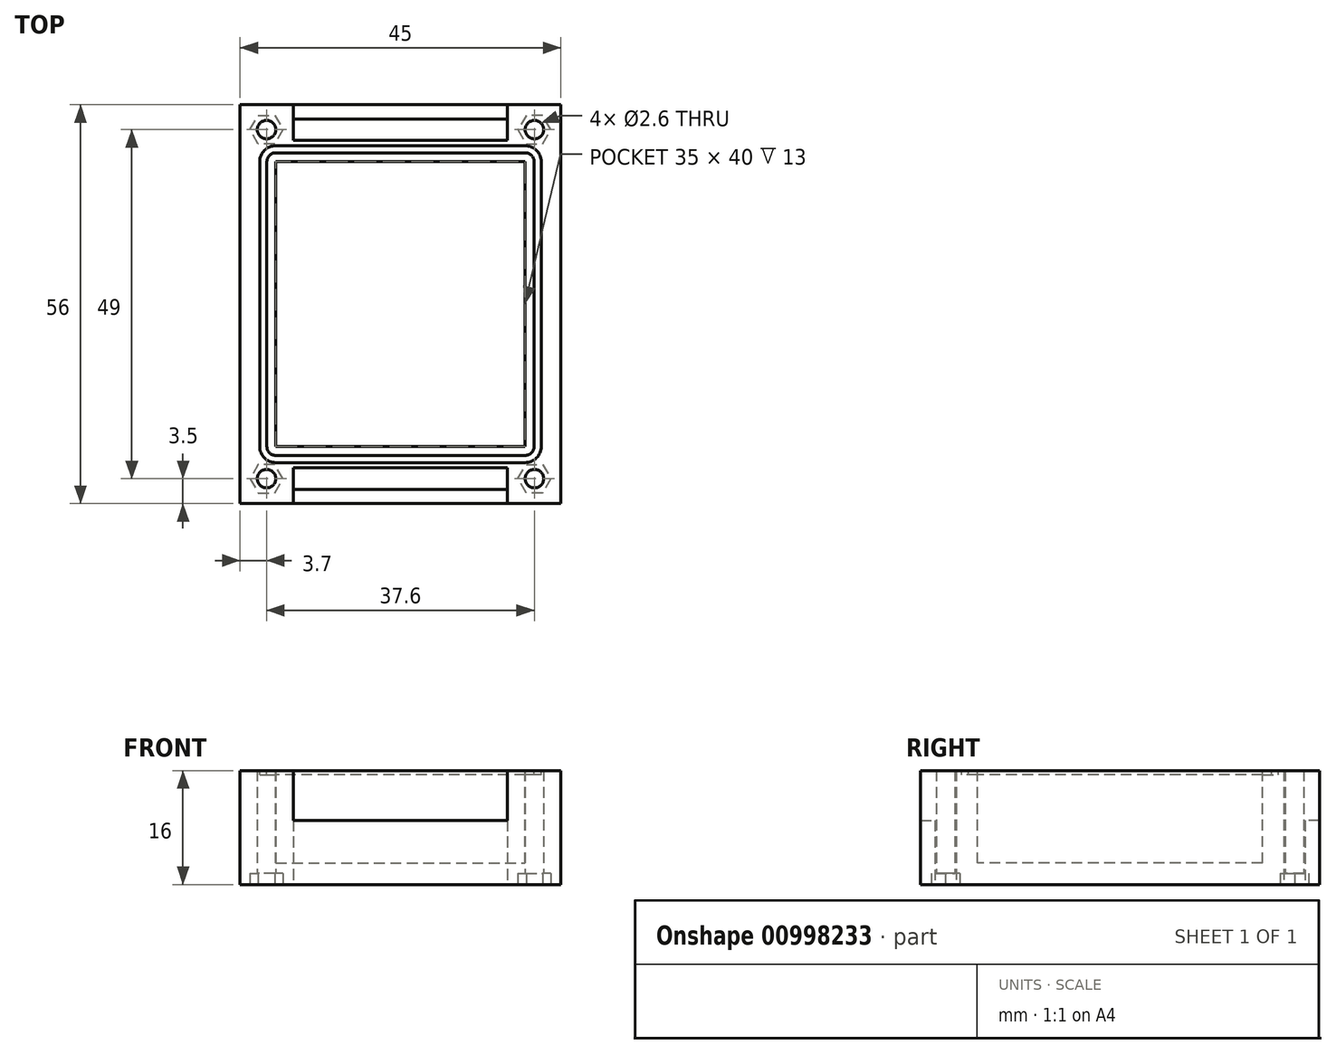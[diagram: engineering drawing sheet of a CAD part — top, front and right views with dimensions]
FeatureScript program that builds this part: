
annotation { "Feature Type Name" : "Feature", "Feature Type Description" : "" }
export const myFeature = defineFeature(function(context is Context, id is Id, definition is map)
    precondition{}
    {
        {
            var Q0;
            Q0=qCreatedBy(makeId("Top.planeOp"),FACE);
            var Q1;
            Q1=qCreatedBy(makeId("Top.planeOp"),FACE);
            var sketch = newSketch(context, id + "F0", { "sketchPlane" : qUnion([Q0, Q1])});
            skLineSegment(sketch, "E0", {"start": v(0, 23) * mm, "end": v(15, 23) * mm});
            skLineSegment(sketch, "E1", {"start": v(22.5, 28) * mm, "end": v(22.5, 0) * mm});
            skLineSegment(sketch, "E2", {"start": v(0, 23) * mm, "end": v(0, 0) * mm});
            skLineSegment(sketch, "E3", {"start": v(0, 28) * mm, "end": v(0, 26) * mm});
            skLineSegment(sketch, "E4", {"start": v(0, 26) * mm, "end": v(15, 26) * mm});
            skLineSegment(sketch, "E5", {"start": v(15, 23) * mm, "end": v(15, 26) * mm});
            skLineSegment(sketch, "E6", {"start": v(0, 28) * mm, "end": v(22.5, 28) * mm});
            skLineSegment(sketch, "E7", {"start": v(22.5, 0) * mm, "end": v(0, 0) * mm});
            skPoint(sketch, "E8.orphan", {"position": v(0, 0) * mm});
            skSolve(sketch);
        }
        {
            var Q0;
            Q0 = qSketchRegion(id + "F0", true);
            extrude(context, id + "F1", {"entities" : qUnion([Q0]), "depth" : 16 * mm, "offsetDistance" : 25 * mm});
        }
        {
            var Q0;
            Q0=makeQuery(id+"F1.opExtrude","CAP_FACE",FACE,{"disambiguationData":[OSD([sQuery(id+"F0.wireOp",EDGE,"E0"),sQuery(id+"F0.wireOp",EDGE,"zLziVwUA-pqAk-qgk8-8UCK-iLvItPBVNLMh"),sQuery(id+"F0.wireOp",EDGE,"wFU1Dp7x-DsTY-6w94-6RtG-82Ve4ZeFUhQ2"),sQuery(id+"F0.wireOp",EDGE,"E1"),sQuery(id+"F0.wireOp",EDGE,"1tPFTLfK-o8Uq-jivp-b70F-p9IYyag1Aok2"),sQuery(id+"F0.wireOp",EDGE,"YqrB6EEW-OV6K-1aBH-CTyA-Jv0BLjLknPQv"),sQuery(id+"F0.wireOp",EDGE,"oTJ8Ghu3-OfHO-qnZb-d6aa-sj9z2I1jH8fg"),sQuery(id+"F0.wireOp",EDGE,"E2")])],"isStart":false});
            var sketch = newSketch(context, id + "F2", { "sketchPlane" : qUnion([Q0])});
            skLineSegment(sketch, "E9.bottom", {"start": v(0, 20) * mm, "end": v(17.5, 20) * mm});
            skLineSegment(sketch, "E9.top", {"start": v(0, 0) * mm, "end": v(17.5, 0) * mm});
            skLineSegment(sketch, "E9.left", {"start": v(0, 20) * mm, "end": v(0, 0) * mm});
            skLineSegment(sketch, "E9.right", {"start": v(17.5, 20) * mm, "end": v(17.5, 0) * mm});
            skSolve(sketch);
        }
        {
            var Q0;
            Q0 = qSketchRegion(id + "F2", true);
            extrude(context, id + "F3", {"entities" : qUnion([Q0]), "operationType" : NewBodyOperationType.REMOVE, "oppositeDirection" : true, "depth" : 13 * mm, "offsetDistance" : 25 * mm});
        }
        {
            var Q0;
            {var subQ0=makeQuery(id+"F1.opExtrude","CAP_FACE",FACE,{"disambiguationData":[OSD([sQuery(id+"F0.wireOp",EDGE,"E0"),sQuery(id+"F0.wireOp",EDGE,"zLziVwUA-pqAk-qgk8-8UCK-iLvItPBVNLMh"),sQuery(id+"F0.wireOp",EDGE,"wFU1Dp7x-DsTY-6w94-6RtG-82Ve4ZeFUhQ2"),sQuery(id+"F0.wireOp",EDGE,"E1"),sQuery(id+"F0.wireOp",EDGE,"1tPFTLfK-o8Uq-jivp-b70F-p9IYyag1Aok2"),sQuery(id+"F0.wireOp",EDGE,"YqrB6EEW-OV6K-1aBH-CTyA-Jv0BLjLknPQv"),sQuery(id+"F0.wireOp",EDGE,"oTJ8Ghu3-OfHO-qnZb-d6aa-sj9z2I1jH8fg"),sQuery(id+"F0.wireOp",EDGE,"E2")])],"isStart":false});Q0=makeQuery(id+"F12.boolean.opBoolean","MERGE",FACE,{"derivedFrom":[subQ0,makeQuery(id+"F12.opPattern","COPY",FACE,{"derivedFrom":subQ0,"instanceName":"1"})]});}
            var sketch = newSketch(context, id + "F4", { "sketchPlane" : qUnion([Q0])});
            skLineSegment(sketch, "E10.bottom", {"start": v(0, 22.25) * mm, "end": v(17.5, 22.25) * mm});
            skArc(sketch, "E11", {"start": v(18.75, 20) * mm, "mid": v(18.38, 20.88) * mm, "end": v(17.5, 21.25) * mm});
            skArc(sketch, "E12", {"start": v(19.75, 20) * mm, "mid": v(19.1, 21.6) * mm, "end": v(17.5, 22.25) * mm});
            skLineSegment(sketch, "E13", {"start": v(17.5, 21.25) * mm, "end": v(0, 21.25) * mm});
            skLineSegment(sketch, "E14", {"start": v(18.75, 20) * mm, "end": v(18.75, 0) * mm});
            skLineSegment(sketch, "E15", {"start": v(19.75, 20) * mm, "end": v(19.75, 0) * mm});
            skLineSegment(sketch, "E16", {"start": v(0, 22.25) * mm, "end": v(0, 21.25) * mm});
            skLineSegment(sketch, "E17", {"start": v(19.75, 0) * mm, "end": v(18.75, 0) * mm});
            skSolve(sketch);
        }
        {
            var Q0;
            Q0 = qSketchRegion(id + "F4", true);
            extrude(context, id + "F5", {"entities" : qUnion([Q0]), "operationType" : NewBodyOperationType.REMOVE, "oppositeDirection" : true, "depth" : .6 * mm, "offsetDistance" : 25 * mm});
        }
        {
            var Q0;
            {var subQ0=makeQuery(id+"F1.opExtrude","CAP_FACE",FACE,{"disambiguationData":[OSD([sQuery(id+"F0.wireOp",EDGE,"E0"),sQuery(id+"F0.wireOp",EDGE,"E1"),sQuery(id+"F0.wireOp",EDGE,"oTJ8Ghu3-OfHO-qnZb-d6aa-sj9z2I1jH8fg"),sQuery(id+"F0.wireOp",EDGE,"E2"),sQuery(id+"F0.wireOp",EDGE,"E3"),sQuery(id+"F0.wireOp",EDGE,"E4"),sQuery(id+"F0.wireOp",EDGE,"E5"),sQuery(id+"F0.wireOp",EDGE,"Zl3f4Z5Q-yM6C-ffHE-Njlt-vzNsvvNb8iaK"),sQuery(id+"F0.wireOp",EDGE,"fbViNYte-NkZI-zoeq-aq0m-hkNtb6oqrqdO"),sQuery(id+"F0.wireOp",EDGE,"qfmNc8zk-el2u-9pkF-pBeT-ObQ48wad9USP"),sQuery(id+"F0.wireOp",EDGE,"E6"),sQuery(id+"F0.wireOp",EDGE,"2uNglbtt-g0ze-XEj7-sdbv-NYKCwFkJiIXs")])],"isStart":true});Q0=makeQuery(id+"F12.boolean.opBoolean","MERGE",FACE,{"derivedFrom":[subQ0,makeQuery(id+"F12.opPattern","COPY",FACE,{"derivedFrom":subQ0,"instanceName":"1"})]});}
            var sketch = newSketch(context, id + "F6", { "sketchPlane" : qUnion([Q0])});
            skCircle(sketch, "E18", {"center": v(18.8, -24.5) * mm, "radius": 2.3 * mm, "construction": true});
            skLineSegment(sketch, "E19.0", {"start": v(21.1, -24.5) * mm, "end": v(19.95, -26.5) * mm});
            skLineSegment(sketch, "E19.1", {"start": v(19.95, -26.5) * mm, "end": v(17.65, -26.5) * mm});
            skLineSegment(sketch, "E19.2", {"start": v(17.65, -26.5) * mm, "end": v(16.5, -24.5) * mm});
            skLineSegment(sketch, "E19.3", {"start": v(16.5, -24.5) * mm, "end": v(17.65, -22.5) * mm});
            skLineSegment(sketch, "E19.4", {"start": v(17.65, -22.5) * mm, "end": v(19.95, -22.5) * mm});
            skLineSegment(sketch, "E19.5", {"start": v(19.95, -22.5) * mm, "end": v(21.1, -24.5) * mm});
            skPoint(sketch, "E20", {"position": v(15, -24.5) * mm});
            skSolve(sketch);
        }
        {
            var Q0;
            Q0 = qSketchRegion(id + "F6", true);
            extrude(context, id + "F7", {"entities" : qUnion([Q0]), "operationType" : NewBodyOperationType.REMOVE, "oppositeDirection" : true, "depth" : 1.6 * mm, "offsetDistance" : 25 * mm});
        }
        {
            var Q0;
            {var subQ0=makeQuery(id+"F1.opExtrude","CAP_FACE",FACE,{"disambiguationData":[OSD([sQuery(id+"F0.wireOp",EDGE,"E0"),sQuery(id+"F0.wireOp",EDGE,"E1"),sQuery(id+"F0.wireOp",EDGE,"E2"),sQuery(id+"F0.wireOp",EDGE,"E3"),sQuery(id+"F0.wireOp",EDGE,"E4"),sQuery(id+"F0.wireOp",EDGE,"E5"),sQuery(id+"F0.wireOp",EDGE,"E6"),sQuery(id+"F0.wireOp",EDGE,"E7")])],"isStart":true});var subQ1=makeQuery(id+"F12.boolean.opBoolean","MERGE",FACE,{"derivedFrom":[subQ0,makeQuery(id+"F12.opPattern","COPY",FACE,{"derivedFrom":subQ0,"instanceName":"1"})]});Q0=makeQuery(id+"F13.boolean.opBoolean","MERGE",FACE,{"derivedFrom":[subQ1,makeQuery(id+"F13.opPattern","COPY",FACE,{"derivedFrom":subQ1,"instanceName":"1"})]});}
            var sketch = newSketch(context, id + "F8", { "sketchPlane" : qUnion([Q0])});
            skPoint(sketch, "E21", {"position": v(18.8, -24.5) * mm});
            skSolve(sketch);
        }
        {
            var Q0;
            Q0=sQuery(id+"F8.wireOp",VERTEX,"E21");
            var Q1;
            Q1=makeQuery(id+"F1.opExtrude","SWEPT_BODY",BODY,{"disambiguationData":[OSD([sQuery(id+"F0.wireOp",EDGE,"E0"),sQuery(id+"F0.wireOp",EDGE,"E1"),sQuery(id+"F0.wireOp",EDGE,"oTJ8Ghu3-OfHO-qnZb-d6aa-sj9z2I1jH8fg"),sQuery(id+"F0.wireOp",EDGE,"E2"),sQuery(id+"F0.wireOp",EDGE,"E3"),sQuery(id+"F0.wireOp",EDGE,"E4"),sQuery(id+"F0.wireOp",EDGE,"E5"),sQuery(id+"F0.wireOp",EDGE,"Zl3f4Z5Q-yM6C-ffHE-Njlt-vzNsvvNb8iaK"),sQuery(id+"F0.wireOp",EDGE,"fbViNYte-NkZI-zoeq-aq0m-hkNtb6oqrqdO"),sQuery(id+"F0.wireOp",EDGE,"qfmNc8zk-el2u-9pkF-pBeT-ObQ48wad9USP"),sQuery(id+"F0.wireOp",EDGE,"E6"),sQuery(id+"F0.wireOp",EDGE,"2uNglbtt-g0ze-XEj7-sdbv-NYKCwFkJiIXs")])]});
            hole(context, id + "F9", {"style" : HoleStyle.SIMPLE, "endStyle" : HoleEndStyle.THROUGH, "standardTappedOrClearance" : lookupTablePath({ "fit" : "Loose", "standard" : "ISO", "size" : "M2", "type" : "Clearance" }), "standardBlindInLast" : lookupTablePath({ "fit" : "Loose", "standard" : "ISO", "engagement" : "75%", "pitch" : "0.25 mm", "size" : "M2", "type" : "Clearance & tapped" }), "holeDiameter" : 2.6 * mm, "majorDiameter" : 5 * mm, "isTappedThrough" : true, "tappedDepth" : 12 * mm, "tapClearance" : 3, "locations" : qUnion([Q0]), "scope" : qUnion([Q1])});
        }
        {
            var Q0;
            {var subQ0=sQuery(id+"F0.wireOp",EDGE,"E7");var subQ1=sQuery(id+"F0.wireOp",EDGE,"E6");var subQ2=sQuery(id+"F0.wireOp",EDGE,"E5");var subQ3=sQuery(id+"F0.wireOp",EDGE,"E4");var subQ4=sQuery(id+"F0.wireOp",EDGE,"E0");var subQ5=sQuery(id+"F0.wireOp",EDGE,"E3");var subQ6=sQuery(id+"F0.wireOp",EDGE,"E1");var subQ7=sQuery(id+"F0.wireOp",EDGE,"E2");var subQ8=makeQuery(id+"F5.boolean.opBoolean","SPLIT",FACE,{"disambiguationData":[TD([makeQuery(id+"F1.opExtrude","SWEPT_FACE",FACE,{"disambiguationData":[OSD([subQ4])]})])],"derivedFrom":makeQuery(id+"F1.opExtrude","CAP_FACE",FACE,{"disambiguationData":[OSD([subQ4,subQ6,subQ7,subQ5,subQ3,subQ2,subQ1,subQ0])],"isStart":false})});var subQ9=makeQuery(id+"F12.boolean.opBoolean","MERGE",FACE,{"derivedFrom":[subQ8,makeQuery(id+"F12.opPattern","COPY",FACE,{"derivedFrom":subQ8,"instanceName":"1"})]});Q0=makeQuery(id+"F13.boolean.opBoolean","MERGE",FACE,{"derivedFrom":[subQ9,makeQuery(id+"F13.opPattern","COPY",FACE,{"derivedFrom":subQ9,"instanceName":"1"})]});}
            var sketch = newSketch(context, id + "F10", { "sketchPlane" : qUnion([Q0])});
            skLineSegment(sketch, "E22.bottom", {"start": v(0, 30.37) * mm, "end": v(15, 30.37) * mm});
            skLineSegment(sketch, "E22.top", {"start": v(0, 26) * mm, "end": v(15, 26) * mm});
            skLineSegment(sketch, "E22.left", {"start": v(0, 30.37) * mm, "end": v(0, 26) * mm});
            skLineSegment(sketch, "E22.right", {"start": v(15, 30.37) * mm, "end": v(15, 26) * mm});
            skSolve(sketch);
        }
        {
            var Q0;
            Q0 = qSketchRegion(id + "F10", true);
            extrude(context, id + "F11", {"entities" : qUnion([Q0]), "operationType" : NewBodyOperationType.REMOVE, "oppositeDirection" : true, "depth" : 7 * mm, "offsetDistance" : 25 * mm});
        }
        {
            var Q0;
            Q0=makeQuery(id+"F1.opExtrude","SWEPT_BODY",BODY,{"disambiguationData":[OSD([sQuery(id+"F0.wireOp",EDGE,"E0"),sQuery(id+"F0.wireOp",EDGE,"zLziVwUA-pqAk-qgk8-8UCK-iLvItPBVNLMh"),sQuery(id+"F0.wireOp",EDGE,"wFU1Dp7x-DsTY-6w94-6RtG-82Ve4ZeFUhQ2"),sQuery(id+"F0.wireOp",EDGE,"E1"),sQuery(id+"F0.wireOp",EDGE,"1tPFTLfK-o8Uq-jivp-b70F-p9IYyag1Aok2"),sQuery(id+"F0.wireOp",EDGE,"YqrB6EEW-OV6K-1aBH-CTyA-Jv0BLjLknPQv"),sQuery(id+"F0.wireOp",EDGE,"oTJ8Ghu3-OfHO-qnZb-d6aa-sj9z2I1jH8fg"),sQuery(id+"F0.wireOp",EDGE,"E2")])]});
            var Q1;
            Q1=qCreatedBy(makeId("Right.planeOp"),FACE);
            mirror(context, id + "F12", {"operationType" : NewBodyOperationType.ADD, "entities" : qUnion([Q0]), "mirrorPlane" : qUnion([Q1])});
        }
        {
            var Q0;
            Q0=makeQuery(id+"F1.opExtrude","SWEPT_BODY",BODY,{"disambiguationData":[OSD([sQuery(id+"F0.wireOp",EDGE,"E0"),sQuery(id+"F0.wireOp",EDGE,"E1"),sQuery(id+"F0.wireOp",EDGE,"E2"),sQuery(id+"F0.wireOp",EDGE,"E3"),sQuery(id+"F0.wireOp",EDGE,"E4"),sQuery(id+"F0.wireOp",EDGE,"E5"),sQuery(id+"F0.wireOp",EDGE,"E6"),sQuery(id+"F0.wireOp",EDGE,"E7")])]});
            var Q1;
            Q1=qCreatedBy(makeId("Front.planeOp"),FACE);
            mirror(context, id + "F13", {"operationType" : NewBodyOperationType.ADD, "entities" : qUnion([Q0]), "mirrorPlane" : qUnion([Q1])});
        }
    });
